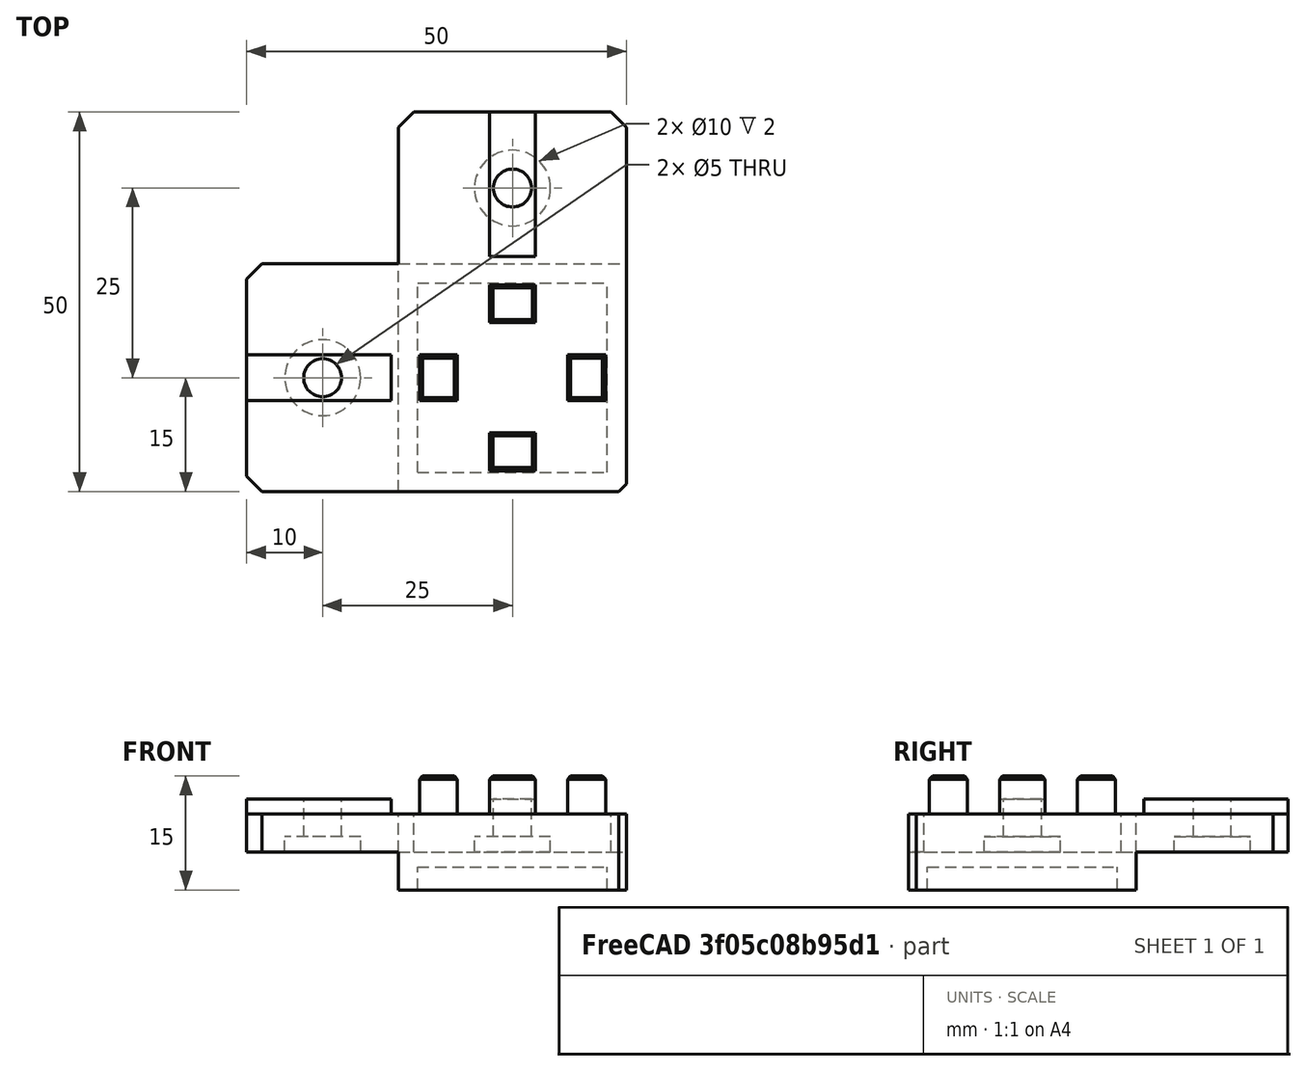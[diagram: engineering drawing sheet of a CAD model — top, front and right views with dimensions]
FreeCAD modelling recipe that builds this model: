
FCSTD DOCUMENT  (FreeCAD 0.18R16146 (Git))
Label: foot-10mm
License: All rights reserved
LicenseURL: http://en.wikipedia.org/wiki/All_rights_reserved
objects: Part::Box×10, Part::Chamfer×7, Part::Cut×5, Part::Cylinder×4, Part::MultiFuse×3
note: 29 computed .brp shape members not serialized (recipe doc carries the construction recipe); baked Part::Feature solids carry a one-line shape summary decoded from their .brp

FEATURE [Part::Box] Box  label="Cube"
  AttacherType = Attacher::AttachEngine3D
  Height = 10
  Length = 30
  Placement = pos=(-15,-15,-10) rot=(0,0,1;0rad)
  Width = 30
FEATURE [Part::Box] Box001  label="Cube001"
  AttacherType = Attacher::AttachEngine3D
  Height = 5
  Length = 6
  Placement = pos=(-3,7.25,0) rot=(0,0,1;0rad)
  Width = 5
FEATURE [Part::Box] Box002  label="Cube002"
  AttacherType = Attacher::AttachEngine3D
  Height = 5
  Length = 6
  Placement = pos=(-3,-12.25,0) rot=(0,0,1;0rad)
  Width = 5
FEATURE [Part::Box] Box003  label="Cube003"
  AttacherType = Attacher::AttachEngine3D
  Height = 5
  Length = 5
  Placement = pos=(7.25,-3,0) rot=(0,0,1;0rad)
  Width = 6
FEATURE [Part::Box] Box004  label="Cube004"
  AttacherType = Attacher::AttachEngine3D
  Height = 5
  Length = 5
  Placement = pos=(-12.25,-3,0) rot=(0,0,1;0rad)
  Width = 6
FEATURE [Part::Box] Box005  label="Cube005"
  AttacherType = Attacher::AttachEngine3D
  Height = 5
  Length = 30
  Placement = pos=(-15,15,-5) rot=(0,0,1;0rad)
  Width = 20
FEATURE [Part::Box] Box006  label="Cube006"
  AttacherType = Attacher::AttachEngine3D
  Height = 5
  Length = 20
  Placement = pos=(-35,-15,-5) rot=(0,0,1;0rad)
  Width = 30
FEATURE [Part::Box] Box007  label="Cube007"
  AttacherType = Attacher::AttachEngine3D
  Height = 2
  Length = 6
  Placement = pos=(-3,16,0) rot=(0,0,1;0rad)
  Width = 19
FEATURE [Part::Box] Box008  label="Cube008"
  AttacherType = Attacher::AttachEngine3D
  Height = 2
  Length = 19
  Placement = pos=(-35,-3,0) rot=(0,0,1;0rad)
  Width = 6
FEATURE [Part::MultiFuse] Fusion
  Shapes = -> [Box008,Box006]
FEATURE [Part::MultiFuse] Fusion001
  Shapes = -> [Box007,Box005]
FEATURE [Part::Cylinder] Cylinder
  Angle = 360
  AttacherType = Attacher::AttachEngine3D
  Height = 10
  Placement = pos=(-25,0,-5) rot=(0,0,1;0rad)
  Radius = 2.5
FEATURE [Part::Cylinder] Cylinder001
  Angle = 360
  AttacherType = Attacher::AttachEngine3D
  Height = 10
  Placement = pos=(0,25,-5) rot=(0,0,1;0rad)
  Radius = 2.5
FEATURE [Part::Cut] Cut
  Base = -> Fusion
  Tool = -> Cylinder
FEATURE [Part::Cut] Cut001
  Base = -> Fusion001
  Tool = -> Cylinder001
FEATURE [Part::Chamfer] Chamfer
  Base = -> Cut
  Edges = 2 edges r=2: [Edge1,Edge5]
FEATURE [Part::Chamfer] Chamfer001
  Base = -> Cut001
  Edges = 2 edges r=2: [Edge3,Edge15]
FEATURE [Part::Chamfer] Chamfer002
  Base = -> Box002
  Edges = 4 edges r=0.4: [Edge2,Edge6,Edge10,Edge12]
FEATURE [Part::Chamfer] Chamfer003
  Base = -> Box003
  Edges = 4 edges r=0.4: [Edge2,Edge6,Edge10,Edge12]
FEATURE [Part::Chamfer] Chamfer004
  Base = -> Box004
  Edges = 4 edges r=0.4: [Edge2,Edge6,Edge10,Edge12]
FEATURE [Part::Chamfer] Chamfer005
  Base = -> Box001
  Edges = 4 edges r=0.4: [Edge2,Edge6,Edge10,Edge12]
FEATURE [Part::MultiFuse] Fusion002
  Shapes = -> [Chamfer005,Chamfer004,Chamfer003,Chamfer002,Chamfer001,Chamfer,Box]
FEATURE [Part::Cylinder] Cylinder002
  Angle = 360
  AttacherType = Attacher::AttachEngine3D
  Height = 2
  Placement = pos=(0,25,-5) rot=(0,0,1;0rad)
  Radius = 5
FEATURE [Part::Cylinder] Cylinder003
  Angle = 360
  AttacherType = Attacher::AttachEngine3D
  Height = 2
  Placement = pos=(-25,0,-5) rot=(0,0,1;0rad)
  Radius = 5
FEATURE [Part::Box] Box009  label="Cube009"
  AttacherType = Attacher::AttachEngine3D
  Height = 3
  Length = 25
  Placement = pos=(-12.5,-12.5,-10) rot=(0,0,1;0rad)
  Width = 25
FEATURE [Part::Cut] Cut002
  Base = -> Fusion002
  Tool = -> Cylinder003
FEATURE [Part::Cut] Cut003
  Base = -> Cut002
  Tool = -> Cylinder002
FEATURE [Part::Chamfer] Chamfer006
  Base = -> Cut003
  Edges = 1 edges r=1: [Edge6]
FEATURE [Part::Cut] Cut004
  Base = -> Chamfer006
  Tool = -> Box009
